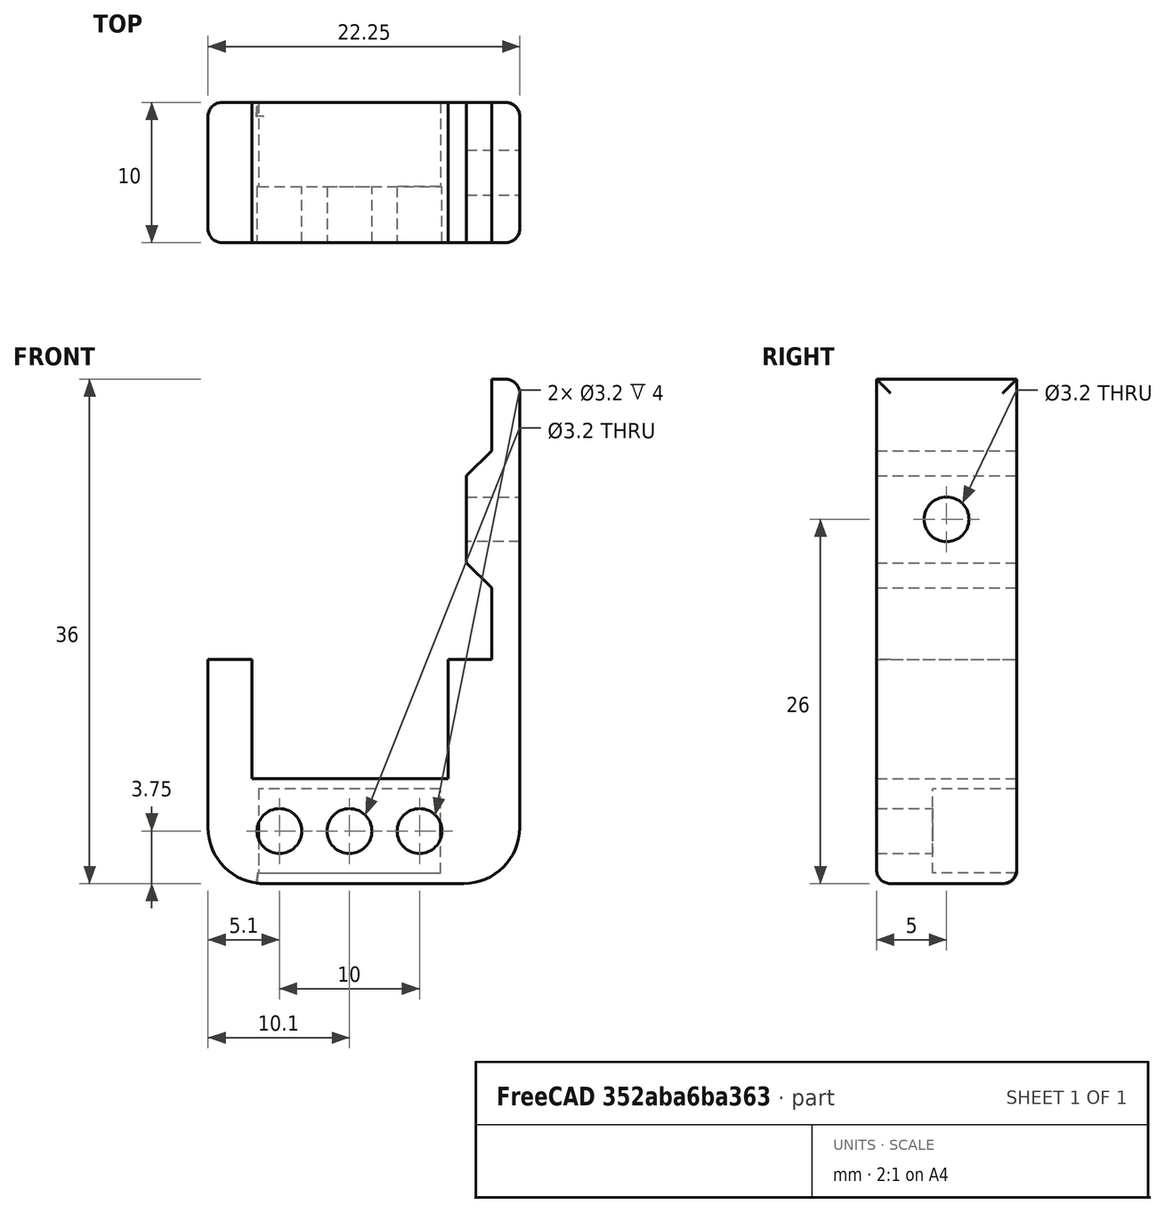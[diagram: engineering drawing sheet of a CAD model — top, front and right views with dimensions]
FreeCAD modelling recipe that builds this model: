
FCSTD DOCUMENT  (FreeCAD 1.0R39109 (Git))
Label: y_switch_holder
License: All rights reserved
LicenseURL: https://en.wikipedia.org/wiki/All_rights_reserved
objects: Sketcher::SketchObject×4, PartDesign::Pocket×3, PartDesign::Fillet×2, Mesh::Feature×1, PartDesign::Pad×1, PartDesign::Body×1, Part::Mirroring×1
note: 28 computed .brp shape members not serialized (recipe doc carries the construction recipe); baked Part::Feature solids carry a one-line shape summary decoded from their .brp

FEATURE [Mesh::Feature] _0x20_v_slot  label="20x20_v-slot"
FEATURE [Sketcher::SketchObject] Sketch
  ArcFitTolerance = 1e-06
  AttachmentSupport = -> [XZ_Plane]
  FullyConstrained = true
  MakeInternals = false
  MapMode = 5
  Placement = pos=(0,0,0) rot=(1,0,0;1.5708rad)
  sketch-geometry (14):
    g0: LineSegment StartX=-10.15 StartY=10 StartZ=0 EndX=-10.15 EndY=4.9 EndZ=0
    g1: LineSegment StartX=-10.15 StartY=4.9 StartZ=0 EndX=-8.35 EndY=3.1 EndZ=0
    g2: LineSegment StartX=-8.35 StartY=3.1 StartZ=0 EndX=-8.35 EndY=-3.1 EndZ=0
    g3: LineSegment StartX=-8.35 StartY=-3.1 StartZ=0 EndX=-10.15 EndY=-4.9 EndZ=0
    g4: LineSegment StartX=-10.15 StartY=-4.9 StartZ=0 EndX=-10.15 EndY=-10 EndZ=0
    g5: LineSegment StartX=-12.15 StartY=-26 StartZ=0 EndX=-12.15 EndY=10 EndZ=0
    g6: LineSegment StartX=-12.15 StartY=10 StartZ=0 EndX=-10.15 EndY=10 EndZ=0
    g7: LineSegment StartX=-12.15 StartY=-26 StartZ=0 EndX=10.1 EndY=-26 EndZ=0
    g8: LineSegment StartX=10.1 StartY=-26 StartZ=0 EndX=10.1 EndY=-10 EndZ=0
    g9: LineSegment StartX=-10.15 StartY=-10 StartZ=0 EndX=-7.025 EndY=-10 EndZ=0
    g10: LineSegment StartX=-7.025 StartY=-10 StartZ=0 EndX=-7.025 EndY=-18.5 EndZ=0
    g11: LineSegment StartX=-7.025 StartY=-18.5 StartZ=0 EndX=6.975 EndY=-18.5 EndZ=0
    g12: LineSegment StartX=6.975 StartY=-18.5 StartZ=0 EndX=6.975 EndY=-10 EndZ=0
    g13: LineSegment StartX=6.975 StartY=-10 StartZ=0 EndX=10.1 EndY=-10 EndZ=0
  constraints (41):
    c: Vertical(g0)
    c: Coincident(g0,g1)
    c: Coincident(g1,g2)
    c: Coincident(g2,g3)
    c: Coincident(g3,g4)
    c: Vertical(g4)
    c: Vertical(g5)
    c: Coincident(g5,g6)
    c: Coincident(g6,g0)
    c: Perpendicular(g3,g1)
    c: DistanceY(g2,g2) = 6.2
    c: DistanceX(g3,g2) = 1.8
    c: DistanceY(g3,g3) = 1.8
    c: DistanceY(g1,g1) = 1.8
    c: DistanceY(g0,g0) = 5.1
    c: DistanceY(g4,g4) = 5.1
    c: DistanceX(g6,g6) = 2
    c: Perpendicular(g0,g6)
    c: DistanceY(g5,g5) = 36
    c: Symmetric(g2,g1,g-1)
    c: DistanceX(g3,g-1) = 10.15
    c: Coincident(g5,g7)
    c: Horizontal(g7)
    c: Coincident(g7,g8)
    c: Parallel(g8,g5)
    c: DistanceX(g4,g8) = 20.25
    c: Coincident(g4,g9)
    c: Horizontal(g9)
    c: Coincident(g9,g10)
    c: Vertical(g10)
    c: Coincident(g10,g11)
    c: Coincident(g11,g12)
    c: Vertical(g12)
    c: Coincident(g12,g13)
    c: Coincident(g13,g8)
    c: Equal(g13,g9)
    c: Parallel(g9,g13)
    c: Parallel(g13,g11)
    c: DistanceX(g11,g11) = 14
    c: DistanceY(g12,g12) = 8.5
    c: DistanceY(g9,g12) = 0
FEATURE [PartDesign::Pad] Pad  label="Body001"
  Direction = (0,-1,2e-16)
  Length = 10
  Length2 = 10
  Placement = pos=(0,0,0) rot=(1,0,0;1.5708rad)
  Profile = -> Sketch
  ReferenceAxis = -> Sketch [N_Axis]
  Refine = true
  Reversed = true
  Suppressed = false
  Type = 0
FEATURE [Sketcher::SketchObject] Sketch001
  ArcFitTolerance = 1e-06
  AttachmentSupport = -> [Pad]
  ExternalGeometry = -> [Pad]
  FullyConstrained = true
  MakeInternals = false
  MapMode = 5
  Placement = pos=(-12.15,0,0) rot=(0.707107,0,-0.707107;3.14159rad)
  sketch-geometry (2):
    g0: Circle CenterX=0 CenterY=-5 CenterZ=0 NormalX=0 NormalY=0 NormalZ=1 AngleXU=0 Radius=1.6
    g1: GeomPoint X=0 Y=-10 Z=0
  constraints (4):
    c: Diameter(g0) = 3.2
    c: PointOnObject(g0,g-2)
    c: PointOnObject(g1,g-4)
    c: Symmetric(g-1,g1,g0)
FEATURE [PartDesign::Pocket] Pocket  label="SlotMountHoles"
  BaseFeature = -> Pad
  Direction = (1,0,2e-16)
  Length = 5
  Length2 = 5
  Placement = pos=(0,0,0) rot=(1,0,0;1.5708rad)
  Profile = -> Sketch001
  ReferenceAxis = -> Sketch001 [N_Axis]
  Refine = true
  Suppressed = false
  Type = 0
FEATURE [Sketcher::SketchObject] Sketch002
  ArcFitTolerance = 1e-06
  AttachmentSupport = -> [Pocket]
  ExternalGeometry = -> [Pocket]
  FullyConstrained = true
  MakeInternals = false
  MapMode = 5
  Placement = pos=(0,10,0) rot=(-1,0,0;1.5708rad)
  sketch-geometry (9):
    g0: LineSegment StartX=-6.5 StartY=19.25 StartZ=0 EndX=6.5 EndY=19.25 EndZ=0
    g1: LineSegment StartX=6.5 StartY=19.25 StartZ=0 EndX=6.5 EndY=25.25 EndZ=0
    g2: LineSegment StartX=6.5 StartY=25.25 StartZ=0 EndX=-6.5 EndY=25.25 EndZ=0
    g3: LineSegment StartX=-6.5 StartY=25.25 StartZ=0 EndX=-6.5 EndY=19.25 EndZ=0
    g4: GeomPoint [constr] X=0 Y=22.25 Z=0
    g5: LineSegment [constr] StartX=-6.5 StartY=25.25 StartZ=0 EndX=-6.5 EndY=26 EndZ=0
    g6: LineSegment [constr] StartX=-6.5 StartY=19.25 StartZ=0 EndX=-6.5 EndY=18.5 EndZ=0
    g7: LineSegment [constr] StartX=6.5 StartY=25.25 StartZ=0 EndX=6.5 EndY=26 EndZ=0
    g8: LineSegment [constr] StartX=6.5 StartY=19.25 StartZ=0 EndX=6.5 EndY=18.5 EndZ=0
  constraints (25):
    c: Coincident(g0,g1)
    c: Coincident(g1,g2)
    c: Coincident(g2,g3)
    c: Coincident(g3,g0)
    c: Horizontal(g0)
    c: Horizontal(g2)
    c: Vertical(g1)
    c: Vertical(g3)
    c: Symmetric(g2,g0,g4)
    c: Distance(g1,g3) = 13
    c: Distance(g0,g2) = 6
    c: PointOnObject(g4,g-2)
    c: Vertical(g5)
    c: Coincident(g5,g2)
    c: PointOnObject(g5,g-3)
    c: Vertical(g6)
    c: Coincident(g6,g0)
    c: PointOnObject(g6,g-4)
    c: Vertical(g7)
    c: Coincident(g7,g1)
    c: PointOnObject(g7,g-3)
    c: Vertical(g8)
    c: Coincident(g8,g0)
    c: PointOnObject(g8,g-4)
    c: Equal(g8,g5)
FEATURE [PartDesign::Pocket] Pocket001  label="SwitchBodyCavity"
  BaseFeature = -> Pocket
  Direction = (0,-1,-2e-16)
  Length = 6
  Length2 = 5
  Placement = pos=(0,0,0) rot=(1,0,0;1.5708rad)
  Profile = -> Sketch002
  ReferenceAxis = -> Sketch002 [N_Axis]
  Refine = true
  Suppressed = false
  Type = 0
FEATURE [Sketcher::SketchObject] Sketch003
  ArcFitTolerance = 1e-06
  AttachmentSupport = -> [Pocket001]
  ExternalGeometry = -> [Pocket001]
  FullyConstrained = false
  MakeInternals = false
  MapMode = 5
  Placement = pos=(0,4,1.2e-15) rot=(-1,0,0;1.5708rad)
  sketch-geometry (6):
    g0: Circle CenterX=5e-16 CenterY=22.25 CenterZ=0 NormalX=0 NormalY=0 NormalZ=1 AngleXU=0 Radius=1.6
    g1: LineSegment [constr] StartX=-17.2271 StartY=22.25 StartZ=0 EndX=20.8743 EndY=22.25 EndZ=0
    g2: GeomPoint [constr] X=9e-16 Y=25.25 Z=0
    g3: GeomPoint [constr] X=2e-16 Y=19.25 Z=0
    g4: Circle CenterX=-5 CenterY=22.25 CenterZ=0 NormalX=0 NormalY=0 NormalZ=1 AngleXU=0 Radius=1.6
    g5: Circle CenterX=5 CenterY=22.25 CenterZ=0 NormalX=0 NormalY=0 NormalZ=1 AngleXU=0 Radius=1.6
  constraints (11):
    c: Diameter(g0) = 3.2
    c: Horizontal(g1)
    c: PointOnObject(g0,g1)
    c: Symmetric(g-3,g-3,g2)
    c: Symmetric(g-4,g-4,g3)
    c: Symmetric(g2,g3,g0)
    c: Diameter(g4) = 3.2
    c: PointOnObject(g4,g1)
    c: Diameter(g5) = 3.2
    c: Symmetric(g5,g4,g0)
    c: DistanceX(g4,g0) = 5
FEATURE [PartDesign::Pocket] Pocket002
  BaseFeature = -> Pocket001
  Direction = (0,-1,-2e-16)
  Length = 12
  Length2 = 5
  Placement = pos=(0,0,0) rot=(1,0,0;1.5708rad)
  Profile = -> Sketch003
  ReferenceAxis = -> Sketch003 [N_Axis]
  Refine = true
  Suppressed = false
  Type = 0
FEATURE [PartDesign::Fillet] Fillet
  Base = -> Pocket002 [Edge1,Edge6]
  BaseFeature = -> Pocket002
  Placement = pos=(0,0,0) rot=(1,0,0;1.5708rad)
  Radius = 4
  Refine = true
  SupportTransform = false
  Suppressed = false
  UseAllEdges = false
FEATURE [PartDesign::Fillet] Fillet001
  Base = -> Fillet [Edge4,Edge1,Edge32,Edge12,Edge30,Edge28,Edge25,Edge8,Edge10,Edge6,Edge3]
  BaseFeature = -> Fillet
  Placement = pos=(0,0,0) rot=(1,0,0;1.5708rad)
  Radius = 1
  Refine = true
  SupportTransform = false
  Suppressed = false
  UseAllEdges = false
FEATURE [PartDesign::Body] Body  label="y_switch_holder_L"
  AllowCompound = false
  Group = -> [Sketch,Pad,Sketch001,Pocket,Sketch002,Pocket001,Sketch003,Pocket002,Fillet,Fillet001]
  Origin = -> Origin
  Tip = -> Fillet001
FEATURE [Part::Mirroring] Part__Mirroring  label="y_switch_holder_R"
  Base = (0,0,0)
  Normal = (1,0,0)
  Source = -> Body
